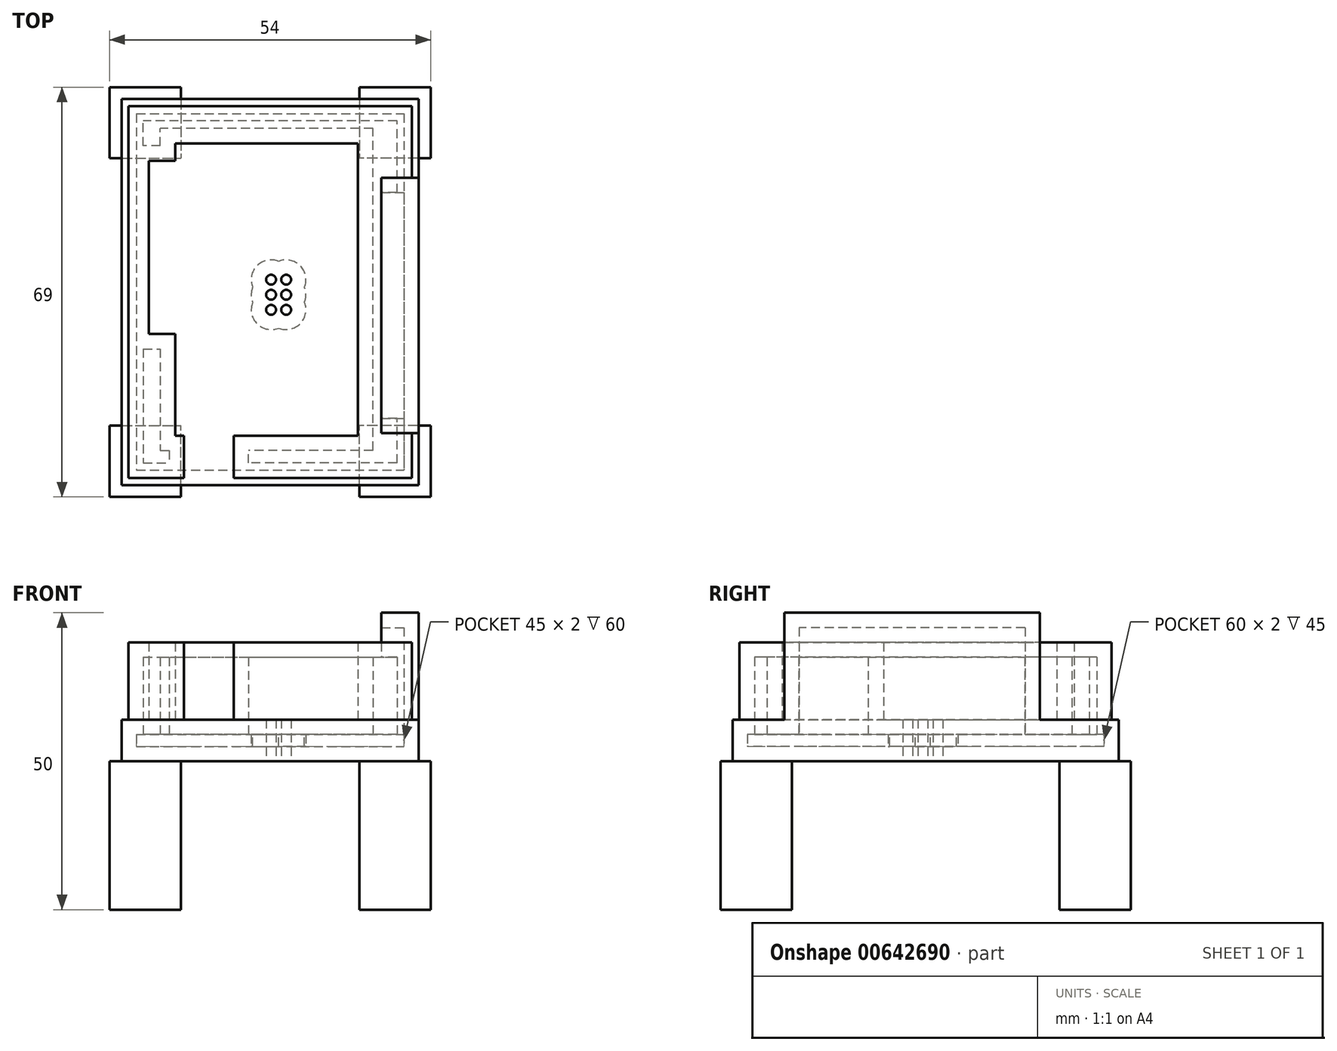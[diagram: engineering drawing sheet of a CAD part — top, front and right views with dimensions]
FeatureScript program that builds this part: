
annotation { "Feature Type Name" : "Feature", "Feature Type Description" : "" }
export const myFeature = defineFeature(function(context is Context, id is Id, definition is map)
    precondition{}
    {
        {
            var Q0;
            Q0=qCreatedBy(makeId("Top.planeOp"),FACE);
            var sketch = newSketch(context, id + "F0", { "sketchPlane" : qUnion([Q0])});
            skLineSegment(sketch, "E0.bottom", {"start": v(-25, 32.5) * mm, "end": v(25, 32.5) * mm});
            skLineSegment(sketch, "E0.top", {"start": v(-25, -32.5) * mm, "end": v(25, -32.5) * mm});
            skLineSegment(sketch, "E0.left", {"start": v(-25, 32.5) * mm, "end": v(-25, -32.5) * mm});
            skLineSegment(sketch, "E0.right", {"start": v(25, 32.5) * mm, "end": v(25, -32.5) * mm});
            skPoint(sketch, "E0.middle", {"position": v(0, 0) * mm});
            skCircle(sketch, "E1", {"center": v(0.16, 2.08) * mm, "radius": 0.83 * mm});
            skCircle(sketch, "E2", {"center": v(0.16, -0.46) * mm, "radius": 0.83 * mm});
            skLineSegment(sketch, "E3", {"start": v(1.43, 5.14) * mm, "end": v(1.43, -5.81) * mm});
            skCircle(sketch, "E4.MirrorC", {"center": v(2.7, 2.08) * mm, "radius": 0.83 * mm});
            skCircle(sketch, "E5.MirrorC", {"center": v(2.7, -0.46) * mm, "radius": 0.83 * mm});
            skCircle(sketch, "E6", {"center": v(0.16, -3) * mm, "radius": 0.83 * mm});
            skCircle(sketch, "E7", {"center": v(2.7, -3) * mm, "radius": 0.83 * mm});
            skLineSegment(sketch, "E8.bottom", {"start": v(18.72, 19.22) * mm, "end": v(25, 19.22) * mm});
            skLineSegment(sketch, "E8.top", {"start": v(18.72, -23.78) * mm, "end": v(25, -23.78) * mm});
            skLineSegment(sketch, "E8.left", {"start": v(18.72, 19.22) * mm, "end": v(18.72, -23.78) * mm});
            skLineSegment(sketch, "E8.right", {"start": v(25, 19.22) * mm, "end": v(25, -23.78) * mm});
            skSolve(sketch);
        }
        {
            var Q0;
            Q0=makeQuery(id+"F0.imprint","IMPRINT",FACE,{"disambiguationData":[TD([[makeQuery(id+"F0.imprint","IMPRINT",EDGE,{"derivedFrom":sQuery(id+"F0.wireOp",EDGE,"E0.bottom")}),-1.0]])]});
            var Q1;
            Q1=sQuery(id+"F0.wireOp",EDGE,"E0.bottom");
            var Q2;
            Q2=sQuery(id+"F0.wireOp",EDGE,"E0.left");
            var Q3;
            Q3=sQuery(id+"F0.wireOp",EDGE,"E0.top");
            var Q4;
            Q4=sQuery(id+"F0.wireOp",EDGE,"E0.right");
            extrude(context, id + "F1", {"entities" : qUnion([Q0]), "surfaceEntities" : qUnion([Q1, Q2, Q3, Q4]), "depth" : 7 * mm, "offsetDistance" : 25 * mm});
        }
        {
            var Q0;
            Q0=qCreatedBy(makeId("Top.planeOp"),FACE);
            var sketch = newSketch(context, id + "F2", { "sketchPlane" : qUnion([Q0])});
            skLineSegment(sketch, "E9.bottom", {"start": v(-23.86, 31.3) * mm, "end": v(23.86, 31.3) * mm});
            skLineSegment(sketch, "E9.top", {"start": v(-23.86, -31.3) * mm, "end": v(23.86, -31.3) * mm});
            skLineSegment(sketch, "E9.left", {"start": v(-23.86, 31.3) * mm, "end": v(-23.86, -31.3) * mm});
            skLineSegment(sketch, "E9.right", {"start": v(23.86, 31.3) * mm, "end": v(23.86, -31.3) * mm});
            skLineSegment(sketch, "E10.bottom", {"start": v(-15.98, 25.02) * mm, "end": v(14.8, 25.02) * mm});
            skLineSegment(sketch, "E10.top", {"start": v(-15.98, -24.18) * mm, "end": v(14.8, -24.18) * mm});
            skLineSegment(sketch, "E10.left", {"start": v(-15.98, 25.02) * mm, "end": v(-15.98, -24.18) * mm});
            skLineSegment(sketch, "E10.right", {"start": v(14.8, 25.02) * mm, "end": v(14.8, -24.18) * mm});
            skLineSegment(sketch, "E11.bottom", {"start": v(-14.5, -21.5) * mm, "end": v(-6.15, -21.5) * mm});
            skLineSegment(sketch, "E11.top", {"start": v(-14.5, -31.3) * mm, "end": v(-6.15, -31.3) * mm});
            skLineSegment(sketch, "E11.left", {"start": v(-14.5, -21.5) * mm, "end": v(-14.5, -31.3) * mm});
            skLineSegment(sketch, "E11.right", {"start": v(-6.15, -21.5) * mm, "end": v(-6.15, -31.3) * mm});
            skLineSegment(sketch, "E12.bottom", {"start": v(-20.39, 22.1) * mm, "end": v(-12.69, 22.1) * mm});
            skLineSegment(sketch, "E12.top", {"start": v(-20.39, -7.08) * mm, "end": v(-12.69, -7.08) * mm});
            skLineSegment(sketch, "E12.left", {"start": v(-20.39, 22.1) * mm, "end": v(-20.39, -7.08) * mm});
            skLineSegment(sketch, "E12.right", {"start": v(-12.69, 22.1) * mm, "end": v(-12.69, -7.08) * mm});
            skSolve(sketch);
        }
        {
            var Q0;
            Q0=makeQuery(id+"F2.imprint","IMPRINT",FACE,{"disambiguationData":[TD([[makeQuery(id+"F2.imprint","IMPRINT",EDGE,{"derivedFrom":sQuery(id+"F2.wireOp",EDGE,"E9.bottom")}),-1.0]])]});
            var Q1;
            Q1=sQuery(id+"F2.wireOp",EDGE,"E9.left");
            var Q2;
            Q2=sQuery(id+"F2.wireOp",EDGE,"E9.bottom");
            var Q3;
            Q3=sQuery(id+"F2.wireOp",EDGE,"E9.right");
            var Q4;
            Q4=sQuery(id+"F2.wireOp",EDGE,"E9.top");
            var Q5;
            Q5=sQuery(id+"F2.wireOp",EDGE,"E10.top");
            var Q6;
            Q6=sQuery(id+"F2.wireOp",EDGE,"E10.right");
            var Q7;
            Q7=sQuery(id+"F2.wireOp",EDGE,"E10.bottom");
            var Q8;
            Q8=sQuery(id+"F2.wireOp",EDGE,"E10.left");
            extrude(context, id + "F3", {"entities" : qUnion([Q0]), "operationType" : NewBodyOperationType.ADD, "surfaceEntities" : qUnion([Q1, Q2, Q3, Q4, Q5, Q6, Q7, Q8]), "depth" : 20 * mm, "offsetDistance" : 25 * mm});
        }
        {
            var Q0;
            Q0=makeQuery(id+"F0.imprint","IMPRINT",FACE,{"disambiguationData":[TD([[makeQuery(id+"F0.imprint","IMPRINT",EDGE,{"derivedFrom":sQuery(id+"F0.wireOp",EDGE,"E8.bottom")}),-1.0]])]});
            extrude(context, id + "F4", {"entities" : qUnion([Q0]), "operationType" : NewBodyOperationType.ADD, "depth" : 25 * mm, "offsetDistance" : 25 * mm});
        }
        {
            var Q0;
            Q0=makeQuery(id+"F4.opExtrude","SWEPT_FACE",FACE,{"disambiguationData":[OSD([sQuery(id+"F0.wireOp",EDGE,"E8.left")])]});
            shell(context, id + "F5", {"entities" : qUnion([Q0]), "thickness" : 2.5 * mm});
        }
        {
            var Q0;
            Q0=qCreatedBy(makeId("Top.planeOp"),FACE);
            var sketch = newSketch(context, id + "F6", { "sketchPlane" : qUnion([Q0])});
            skLineSegment(sketch, "E13.bottom", {"start": v(-27, 34.5) * mm, "end": v(-15, 34.5) * mm});
            skLineSegment(sketch, "E13.top", {"start": v(-27, 22.5) * mm, "end": v(-15, 22.5) * mm});
            skLineSegment(sketch, "E13.left", {"start": v(-27, 34.5) * mm, "end": v(-27, 22.5) * mm});
            skLineSegment(sketch, "E13.right", {"start": v(-15, 34.5) * mm, "end": v(-15, 22.5) * mm});
            skLineSegment(sketch, "E14.MirrorCS", {"start": v(27, 22.5) * mm, "end": v(15, 22.5) * mm});
            skLineSegment(sketch, "E15.MirrorCS", {"start": v(27, 34.5) * mm, "end": v(27, 22.5) * mm});
            skLineSegment(sketch, "E16.MirrorCS", {"start": v(27, 34.5) * mm, "end": v(15, 34.5) * mm});
            skLineSegment(sketch, "E17.MirrorCS", {"start": v(15, 34.5) * mm, "end": v(15, 22.5) * mm});
            skLineSegment(sketch, "E18.MirrorCS", {"start": v(-27, -22.5) * mm, "end": v(-15, -22.5) * mm});
            skLineSegment(sketch, "E19.MirrorCS", {"start": v(-27, -34.5) * mm, "end": v(-27, -22.5) * mm});
            skLineSegment(sketch, "E20.MirrorCS", {"start": v(-27, -34.5) * mm, "end": v(-15, -34.5) * mm});
            skLineSegment(sketch, "E21.MirrorCS", {"start": v(-15, -34.5) * mm, "end": v(-15, -22.5) * mm});
            skLineSegment(sketch, "E22.MirrorCS", {"start": v(15, -34.5) * mm, "end": v(15, -22.5) * mm});
            skLineSegment(sketch, "E23.MirrorCS", {"start": v(27, -22.5) * mm, "end": v(15, -22.5) * mm});
            skLineSegment(sketch, "E24.MirrorCS", {"start": v(27, -34.5) * mm, "end": v(27, -22.5) * mm});
            skLineSegment(sketch, "E25.MirrorCS", {"start": v(27, -34.5) * mm, "end": v(15, -34.5) * mm});
            skSolve(sketch);
        }
        {
            var Q0;
            Q0=makeQuery(id+"F6.imprint","IMPRINT",FACE,{"disambiguationData":[TD([[makeQuery(id+"F6.imprint","IMPRINT",EDGE,{"derivedFrom":sQuery(id+"F6.wireOp",EDGE,"E13.bottom")}),-1.0]])]});
            var Q1;
            Q1=makeQuery(id+"F6.imprint","IMPRINT",FACE,{"disambiguationData":[TD([[makeQuery(id+"F6.imprint","IMPRINT",EDGE,{"derivedFrom":sQuery(id+"F6.wireOp",EDGE,"E18.MirrorCS")}),-1.0]])]});
            var Q2;
            Q2=makeQuery(id+"F6.imprint","IMPRINT",FACE,{"disambiguationData":[TD([[makeQuery(id+"F6.imprint","IMPRINT",EDGE,{"derivedFrom":sQuery(id+"F6.wireOp",EDGE,"E22.MirrorCS")}),-1.0]])]});
            var Q3;
            Q3=makeQuery(id+"F6.imprint","IMPRINT",FACE,{"disambiguationData":[TD([[makeQuery(id+"F6.imprint","IMPRINT",EDGE,{"derivedFrom":sQuery(id+"F6.wireOp",EDGE,"E14.MirrorCS")}),-1.0]])]});
            extrude(context, id + "F7", {"entities" : qUnion([Q0, Q1, Q2, Q3]), "operationType" : NewBodyOperationType.ADD, "oppositeDirection" : true, "depth" : 25 * mm, "offsetDistance" : 25 * mm});
        }
    });
